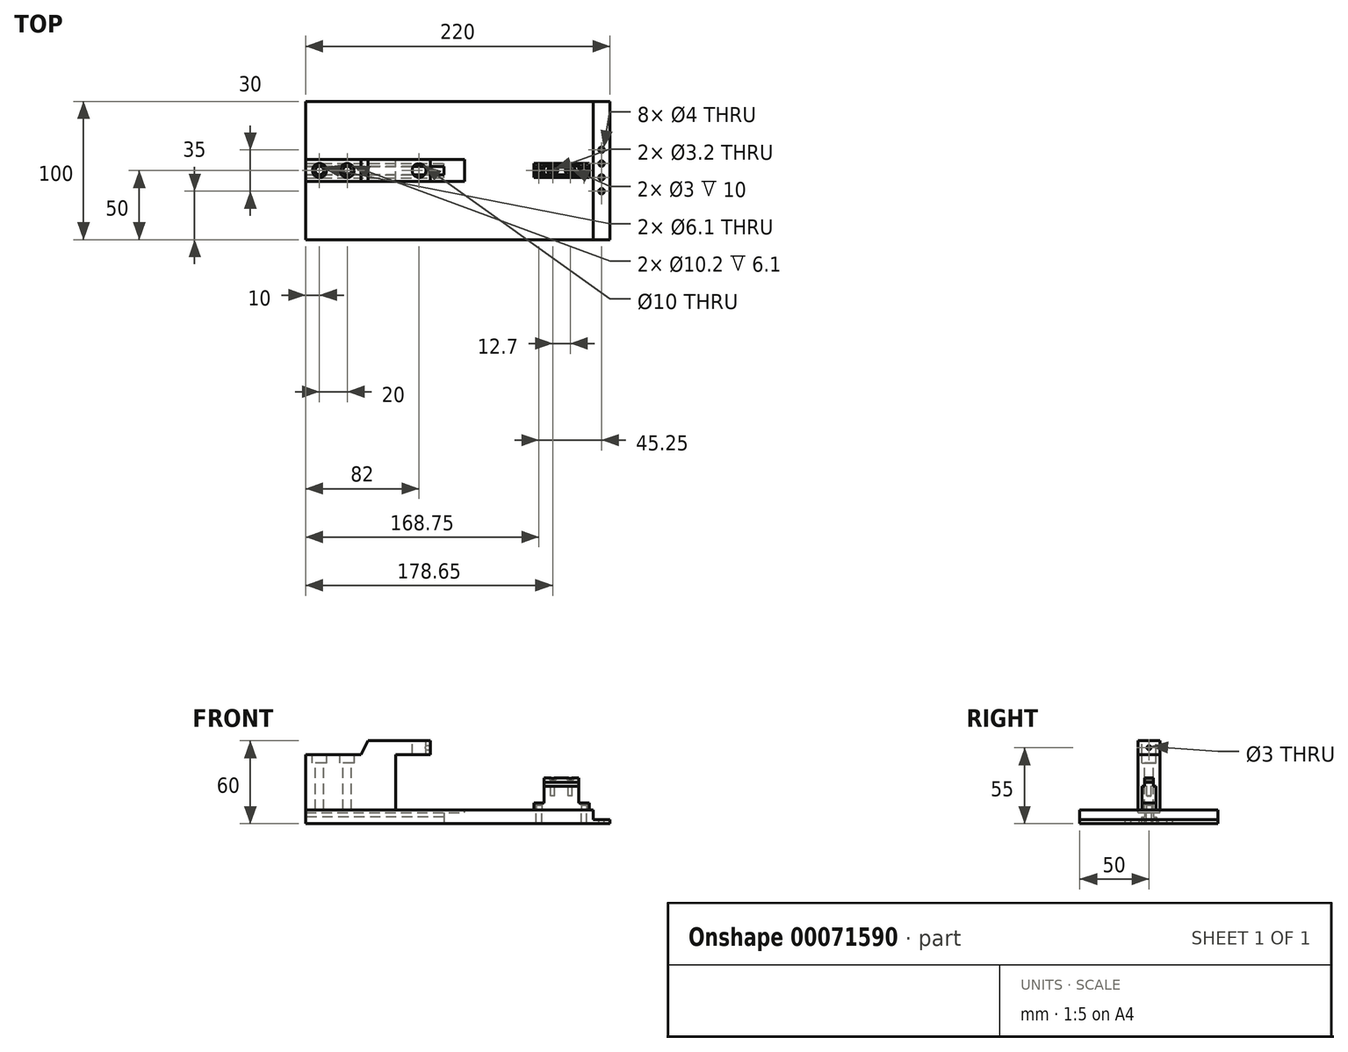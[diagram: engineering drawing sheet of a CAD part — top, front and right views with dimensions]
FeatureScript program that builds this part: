
annotation { "Feature Type Name" : "Feature", "Feature Type Description" : "" }
export const myFeature = defineFeature(function(context is Context, id is Id, definition is map)
    precondition{}
    {
        {
            var Q0;
            Q0=qCreatedBy(makeId("Top.planeOp"),FACE);
            var sketch = newSketch(context, id + "F0", { "sketchPlane" : qUnion([Q0])});
            skLineSegment(sketch, "E0.bottom", {"start": v(0, 0) * mm, "end": v(220, 0) * mm});
            skLineSegment(sketch, "E0.top", {"start": v(0, 100) * mm, "end": v(220, 100) * mm});
            skLineSegment(sketch, "E0.left", {"start": v(0, 0) * mm, "end": v(0, 100) * mm});
            skLineSegment(sketch, "E0.right", {"start": v(220, 0) * mm, "end": v(220, 100) * mm});
            skSolve(sketch);
        }
        {
            var Q0;
            Q0 = qSketchRegion(id + "F0", true);
            extrude(context, id + "F1", {"entities" : qUnion([Q0]), "depth" : 10 * mm});
        }
        {
            var Q0;
            Q0=makeQuery(id+"F1.opExtrude","CAP_FACE",FACE,{"disambiguationData":[OSD([sQuery(id+"F0.wireOp",EDGE,"E0.bottom"),sQuery(id+"F0.wireOp",EDGE,"E0.top"),sQuery(id+"F0.wireOp",EDGE,"E0.left"),sQuery(id+"F0.wireOp",EDGE,"E0.right")])],"isStart":false});
            var sketch = newSketch(context, id + "F2", { "sketchPlane" : qUnion([Q0])});
            skLineSegment(sketch, "E1.bottom", {"start": v(165, 55.18) * mm, "end": v(205, 55.18) * mm});
            skLineSegment(sketch, "E1.top", {"start": v(165, 44.82) * mm, "end": v(205, 44.82) * mm});
            skLineSegment(sketch, "E1.left", {"start": v(165, 55.18) * mm, "end": v(165, 44.82) * mm});
            skLineSegment(sketch, "E1.right", {"start": v(205, 55.18) * mm, "end": v(205, 44.82) * mm});
            skCircle(sketch, "E2", {"center": v(168.75, 50) * mm, "radius": 2 * mm});
            skPoint(sketch, "E2.centerSnap0", {"position": v(165, 50) * mm});
            skCircle(sketch, "E3", {"center": v(201.25, 50) * mm, "radius": 2 * mm});
            skPoint(sketch, "E3.centerSnap0", {"position": v(205, 50) * mm});
            skSolve(sketch);
        }
        {
            var Q0;
            Q0 = qSketchRegion(id + "F2", true);
            extrude(context, id + "F3", {"entities" : qUnion([Q0]), "depth" : 20 * mm});
        }
        {
            var Q0;
            Q0=makeQuery(id+"F3.opExtrude","SWEPT_FACE",FACE,{"disambiguationData":[OSD([sQuery(id+"F2.wireOp",EDGE,"E1.top")])]});
            var sketch = newSketch(context, id + "F4", { "sketchPlane" : qUnion([Q0])});
            skLineSegment(sketch, "E4.bottom", {"start": v(165, 30) * mm, "end": v(172.5, 30) * mm});
            skLineSegment(sketch, "E4.top", {"start": v(165, 15) * mm, "end": v(172.5, 15) * mm});
            skLineSegment(sketch, "E4.left", {"start": v(165, 30) * mm, "end": v(165, 15) * mm});
            skLineSegment(sketch, "E4.right", {"start": v(172.5, 30) * mm, "end": v(172.5, 15) * mm});
            skLineSegment(sketch, "E5.right", {"start": v(205, 30) * mm, "end": v(205, 15) * mm});
            skLineSegment(sketch, "E5.bottom", {"start": v(197.5, 30) * mm, "end": v(205, 30) * mm});
            skLineSegment(sketch, "E5.left", {"start": v(197.5, 30) * mm, "end": v(197.5, 15) * mm});
            skLineSegment(sketch, "E5.top", {"start": v(197.5, 15) * mm, "end": v(205, 15) * mm});
            skSolve(sketch);
        }
        {
            var Q0;
            Q0 = qSketchRegion(id + "F4", true);
            extrude(context, id + "F5", {"entities" : qUnion([Q0]), "operationType" : NewBodyOperationType.REMOVE, "endBound" : BoundingType.THROUGH_ALL, "oppositeDirection" : true, "depth" : 25 * mm});
        }
        {
            var Q0;
            Q0=makeQuery(id+"F3.opExtrude","CAP_FACE",FACE,{"disambiguationData":[OSD([sQuery(id+"F2.wireOp",EDGE,"E1.bottom"),sQuery(id+"F2.wireOp",EDGE,"E1.top"),sQuery(id+"F2.wireOp",EDGE,"E1.left"),sQuery(id+"F2.wireOp",EDGE,"E1.right")])],"isStart":false});
            var sketch = newSketch(context, id + "F6", { "sketchPlane" : qUnion([Q0])});
            skCircle(sketch, "E6", {"center": v(178.65, 50) * mm, "radius": 1.5 * mm});
            skCircle(sketch, "E7", {"center": v(191.35, 50) * mm, "radius": 1.5 * mm});
            skLineSegment(sketch, "E8", {"start": v(172.5, 50) * mm, "end": v(197.5, 50) * mm, "construction": true});
            skSolve(sketch);
        }
        {
            var Q0;
            Q0 = qSketchRegion(id + "F6", true);
            extrude(context, id + "F7", {"entities" : qUnion([Q0]), "operationType" : NewBodyOperationType.REMOVE, "oppositeDirection" : true, "depth" : 10 * mm});
        }
        {
            var Q0;
            Q0=makeQuery(id+"F3.opExtrude","CAP_FACE",FACE,{"disambiguationData":[OSD([sQuery(id+"F2.wireOp",EDGE,"E1.bottom"),sQuery(id+"F2.wireOp",EDGE,"E1.top"),sQuery(id+"F2.wireOp",EDGE,"E1.left"),sQuery(id+"F2.wireOp",EDGE,"E1.right")])],"isStart":false});
            var sketch = newSketch(context, id + "F8", { "sketchPlane" : qUnion([Q0])});
            skLineSegment(sketch, "E9.bottom", {"start": v(172.5, 55.18) * mm, "end": v(197.5, 55.18) * mm});
            skLineSegment(sketch, "E9.top", {"start": v(172.5, 53.17) * mm, "end": v(197.5, 53.17) * mm});
            skLineSegment(sketch, "E9.left", {"start": v(172.5, 55.18) * mm, "end": v(172.5, 53.17) * mm});
            skLineSegment(sketch, "E9.right", {"start": v(197.5, 55.18) * mm, "end": v(197.5, 53.17) * mm});
            skLineSegment(sketch, "E10.bottom", {"start": v(172.5, 44.82) * mm, "end": v(197.5, 44.82) * mm});
            skLineSegment(sketch, "E10.top", {"start": v(172.5, 46.83) * mm, "end": v(197.5, 46.83) * mm});
            skLineSegment(sketch, "E10.left", {"start": v(172.5, 44.82) * mm, "end": v(172.5, 46.82) * mm});
            skLineSegment(sketch, "E10.right", {"start": v(197.5, 44.82) * mm, "end": v(197.5, 46.82) * mm});
            skSolve(sketch);
        }
        {
            var Q0;
            Q0 = qSketchRegion(id + "F8", true);
            extrude(context, id + "F9", {"entities" : qUnion([Q0]), "operationType" : NewBodyOperationType.REMOVE, "oppositeDirection" : true, "depth" : 3 * mm});
        }
        {
            var Q0;
            Q0=makeQuery(id+"F5.boolean.opBoolean","INTERSECT",EDGE,{"derivedFrom":[makeQuery(id+"F3.opExtrude","SWEPT_FACE",FACE,{"disambiguationData":[OSD([sQuery(id+"F2.wireOp",EDGE,"E2")])]}),makeQuery(id+"F5.opExtrude","SWEPT_FACE",FACE,{"disambiguationData":[OSD([sQuery(id+"F4.wireOp",EDGE,"E4.top")])]})]});
            var Q1;
            Q1=makeQuery(id+"F5.boolean.opBoolean","INTERSECT",EDGE,{"derivedFrom":[makeQuery(id+"F3.opExtrude","SWEPT_FACE",FACE,{"disambiguationData":[OSD([sQuery(id+"F2.wireOp",EDGE,"E3")])]}),makeQuery(id+"F5.opExtrude","SWEPT_FACE",FACE,{"disambiguationData":[OSD([sQuery(id+"F4.wireOp",EDGE,"E5.top")])]})]});
            chamfer(context, id + "F10", {"entities" : qUnion([Q0, Q1]), "width" : 1.5 * mm, "tangentPropagation" : true});
        }
        {
            var Q0;
            Q0=makeQuery(id+"F1.opExtrude","CAP_FACE",FACE,{"disambiguationData":[OSD([sQuery(id+"F0.wireOp",EDGE,"E0.bottom"),sQuery(id+"F0.wireOp",EDGE,"E0.top"),sQuery(id+"F0.wireOp",EDGE,"E0.left"),sQuery(id+"F0.wireOp",EDGE,"E0.right")])],"isStart":false});
            var sketch = newSketch(context, id + "F11", { "sketchPlane" : qUnion([Q0])});
            skCircle(sketch, "E11.0", {"center": v(168.75, 50) * mm, "radius": 2 * mm});
            skCircle(sketch, "E11.1", {"center": v(201.25, 50) * mm, "radius": 2 * mm});
            skCircle(sketch, "E12", {"center": v(214, 65) * mm, "radius": 2 * mm});
            skCircle(sketch, "E13", {"center": v(214, 55) * mm, "radius": 2 * mm});
            skCircle(sketch, "E14", {"center": v(214, 45) * mm, "radius": 2 * mm});
            skCircle(sketch, "E15", {"center": v(214, 35) * mm, "radius": 2 * mm});
            skSolve(sketch);
        }
        {
            var Q0;
            Q0 = qSketchRegion(id + "F11", true);
            extrude(context, id + "F12", {"entities" : qUnion([Q0]), "operationType" : NewBodyOperationType.REMOVE, "endBound" : BoundingType.THROUGH_ALL, "oppositeDirection" : true, "depth" : 5 * mm});
        }
        {
            var Q0;
            Q0=makeQuery(id+"F3.opExtrude","CAP_FACE",FACE,{"disambiguationData":[OSD([sQuery(id+"F2.wireOp",EDGE,"E1.bottom"),sQuery(id+"F2.wireOp",EDGE,"E1.top"),sQuery(id+"F2.wireOp",EDGE,"E1.left"),sQuery(id+"F2.wireOp",EDGE,"E1.right"),sQuery(id+"F2.wireOp",EDGE,"E2"),sQuery(id+"F2.wireOp",EDGE,"E3")])],"isStart":false});
            var sketch = newSketch(context, id + "F13", { "sketchPlane" : qUnion([Q0])});
            skLineSegment(sketch, "E16.bottom", {"start": v(172.5, 53.17) * mm, "end": v(197.5, 53.17) * mm});
            skLineSegment(sketch, "E16.top", {"start": v(172.5, 46.83) * mm, "end": v(197.5, 46.83) * mm});
            skLineSegment(sketch, "E16.left", {"start": v(172.5, 53.17) * mm, "end": v(172.5, 46.83) * mm});
            skLineSegment(sketch, "E16.right", {"start": v(197.5, 53.17) * mm, "end": v(197.5, 46.83) * mm});
            skCircle(sketch, "E17", {"center": v(178.65, 50) * mm, "radius": 1.6 * mm});
            skCircle(sketch, "E18", {"center": v(191.35, 50) * mm, "radius": 1.6 * mm});
            skSolve(sketch);
        }
        {
            var Q0;
            Q0 = qSketchRegion(id + "F13", true);
            extrude(context, id + "F14", {"entities" : qUnion([Q0]), "depth" : 3.25 * mm});
        }
        {
            var Q0;
            Q0=makeQuery(id+"F14.opExtrude","CAP_EDGE",EDGE,{"disambiguationData":[OSD([sQuery(id+"F13.wireOp",EDGE,"E17")])],"isStart":false});
            var Q1;
            Q1=makeQuery(id+"F14.opExtrude","CAP_EDGE",EDGE,{"disambiguationData":[OSD([sQuery(id+"F13.wireOp",EDGE,"E18")])],"isStart":false});
            chamfer(context, id + "F15", {"entities" : qUnion([Q0, Q1]), "width" : 2 * mm, "tangentPropagation" : true});
        }
        {
            var Q0;
            Q0=makeQuery(id+"F1.opExtrude","CAP_FACE",FACE,{"disambiguationData":[OSD([sQuery(id+"F0.wireOp",EDGE,"E0.bottom"),sQuery(id+"F0.wireOp",EDGE,"E0.top"),sQuery(id+"F0.wireOp",EDGE,"E0.left"),sQuery(id+"F0.wireOp",EDGE,"E0.right")])],"isStart":true});
            var sketch = newSketch(context, id + "F16", { "sketchPlane" : qUnion([Q0])});
            skLineSegment(sketch, "E19.bottom", {"start": v(0, -46.95) * mm, "end": v(100, -46.95) * mm});
            skLineSegment(sketch, "E19.top", {"start": v(0, -53.05) * mm, "end": v(100, -53.05) * mm});
            skLineSegment(sketch, "E19.left", {"start": v(0, -46.95) * mm, "end": v(0, -53.05) * mm});
            skLineSegment(sketch, "E19.right", {"start": v(100, -46.95) * mm, "end": v(100, -53.05) * mm});
            skSolve(sketch);
        }
        {
            var Q0;
            Q0 = qSketchRegion(id + "F16", true);
            extrude(context, id + "F17", {"entities" : qUnion([Q0]), "operationType" : NewBodyOperationType.REMOVE, "oppositeDirection" : true, "depth" : 25 * mm});
        }
        {
            var Q0;
            Q0=makeQuery(id+"F1.opExtrude","CAP_FACE",FACE,{"disambiguationData":[OSD([sQuery(id+"F0.wireOp",EDGE,"E0.bottom"),sQuery(id+"F0.wireOp",EDGE,"E0.top"),sQuery(id+"F0.wireOp",EDGE,"E0.left"),sQuery(id+"F0.wireOp",EDGE,"E0.right")])],"isStart":true});
            var sketch = newSketch(context, id + "F18", { "sketchPlane" : qUnion([Q0])});
            skLineSegment(sketch, "E20.bottom", {"start": v(0, -44.75) * mm, "end": v(100, -44.75) * mm});
            skLineSegment(sketch, "E20.top", {"start": v(0, -55.25) * mm, "end": v(100, -55.25) * mm});
            skLineSegment(sketch, "E20.left", {"start": v(0, -44.75) * mm, "end": v(0, -55.25) * mm});
            skLineSegment(sketch, "E20.right", {"start": v(100, -44.75) * mm, "end": v(100, -55.25) * mm});
            skSolve(sketch);
        }
        {
            var Q0;
            Q0 = qSketchRegion(id + "F18", true);
            extrude(context, id + "F19", {"entities" : qUnion([Q0]), "operationType" : NewBodyOperationType.REMOVE, "oppositeDirection" : true, "depth" : 5 * mm});
        }
        {
            var Q0;
            Q0=makeQuery(id+"F1.opExtrude","CAP_FACE",FACE,{"disambiguationData":[OSD([sQuery(id+"F0.wireOp",EDGE,"E0.bottom"),sQuery(id+"F0.wireOp",EDGE,"E0.top"),sQuery(id+"F0.wireOp",EDGE,"E0.left"),sQuery(id+"F0.wireOp",EDGE,"E0.right")])],"isStart":false});
            var sketch = newSketch(context, id + "F20", { "sketchPlane" : qUnion([Q0])});
            skCircle(sketch, "E21", {"center": v(168.75, 50) * mm, "radius": 2 * mm});
            skCircle(sketch, "E22", {"center": v(201.25, 50) * mm, "radius": 2 * mm});
            skSolve(sketch);
        }
        {
            var Q0;
            Q0 = qSketchRegion(id + "F20", true);
            extrude(context, id + "F21", {"entities" : qUnion([Q0]), "operationType" : NewBodyOperationType.REMOVE, "endBound" : BoundingType.THROUGH_ALL, "oppositeDirection" : true, "depth" : 25 * mm});
        }
        {
            var Q0;
            Q0=qCreatedBy(makeId("Front.planeOp"),FACE);
            cPlane(context, id + "F22", {"entities" : qUnion([Q0]), "cplaneType" : CPlaneType.OFFSET, "offset" : 50 * mm, "oppositeDirection" : true, "width" : 150 * mm, "height" : 150 * mm});
        }
        {
            var Q0;
            Q0=qCreatedBy(id+"F22.planeOp",FACE);
            var sketch = newSketch(context, id + "F23", { "sketchPlane" : qUnion([Q0])});
            skLineSegment(sketch, "E23", {"start": v(0, 10) * mm, "end": v(0, 50) * mm});
            skLineSegment(sketch, "E24", {"start": v(0, 50) * mm, "end": v(40, 50) * mm});
            skLineSegment(sketch, "E25", {"start": v(40, 50) * mm, "end": v(45, 60) * mm});
            skLineSegment(sketch, "E26", {"start": v(45, 60) * mm, "end": v(90, 60) * mm});
            skLineSegment(sketch, "E27", {"start": v(90, 60) * mm, "end": v(90, 50) * mm});
            skLineSegment(sketch, "E28", {"start": v(90, 50) * mm, "end": v(65, 50) * mm});
            skLineSegment(sketch, "E29", {"start": v(65, 50) * mm, "end": v(65, 10) * mm});
            skLineSegment(sketch, "E30", {"start": v(65, 10) * mm, "end": v(0, 10) * mm});
            skSolve(sketch);
        }
        {
            var Q0;
            Q0 = qSketchRegion(id + "F23", true);
            extrude(context, id + "F24", {"entities" : qUnion([Q0]), "endBound" : BoundingType.SYMMETRIC, "depth" : 16 * mm});
        }
        {
            var Q0;
            Q0=makeQuery(id+"F24.opExtrude","SWEPT_FACE",FACE,{"disambiguationData":[OSD([sQuery(id+"F23.wireOp",EDGE,"E24")])]});
            var sketch = newSketch(context, id + "F25", { "sketchPlane" : qUnion([Q0])});
            skCircle(sketch, "E31", {"center": v(10, 50) * mm, "radius": 3.05 * mm});
            skPoint(sketch, "E31.centerSnap0", {"position": v(0, 50) * mm});
            skCircle(sketch, "E32", {"center": v(30, 50) * mm, "radius": 3.05 * mm});
            skSolve(sketch);
        }
        {
            var Q0;
            Q0 = qSketchRegion(id + "F25", true);
            extrude(context, id + "F26", {"entities" : qUnion([Q0]), "operationType" : NewBodyOperationType.REMOVE, "endBound" : BoundingType.UP_TO_NEXT, "oppositeDirection" : true, "depth" : 25 * mm});
        }
        {
            var Q0;
            Q0=makeQuery(id+"F24.opExtrude","SWEPT_FACE",FACE,{"disambiguationData":[OSD([sQuery(id+"F23.wireOp",EDGE,"E24")])]});
            var sketch = newSketch(context, id + "F27", { "sketchPlane" : qUnion([Q0])});
            skCircle(sketch, "E33", {"center": v(10, 50) * mm, "radius": 5.1 * mm});
            skCircle(sketch, "E34", {"center": v(30, 50) * mm, "radius": 5.1 * mm});
            skSolve(sketch);
        }
        {
            var Q0;
            Q0 = qSketchRegion(id + "F27", true);
            extrude(context, id + "F28", {"entities" : qUnion([Q0]), "operationType" : NewBodyOperationType.REMOVE, "oppositeDirection" : true, "depth" : 6.1 * mm});
        }
        {
            var Q0;
            Q0=makeQuery(id+"F24.opExtrude","SWEPT_FACE",FACE,{"disambiguationData":[OSD([sQuery(id+"F23.wireOp",EDGE,"E26")])]});
            var sketch = newSketch(context, id + "F29", { "sketchPlane" : qUnion([Q0])});
            skCircle(sketch, "E35", {"center": v(82, 50) * mm, "radius": 5 * mm});
            skPoint(sketch, "E35.centerSnap0", {"position": v(90, 50) * mm});
            skSolve(sketch);
        }
        {
            var Q0;
            Q0 = qSketchRegion(id + "F29", true);
            extrude(context, id + "F30", {"entities" : qUnion([Q0]), "operationType" : NewBodyOperationType.REMOVE, "endBound" : BoundingType.UP_TO_NEXT, "oppositeDirection" : true, "depth" : 25 * mm});
        }
        {
            var Q0;
            Q0=makeQuery(id+"F24.opExtrude","SWEPT_FACE",FACE,{"disambiguationData":[OSD([sQuery(id+"F23.wireOp",EDGE,"E27")])]});
            var sketch = newSketch(context, id + "F31", { "sketchPlane" : qUnion([Q0])});
            skCircle(sketch, "E36", {"center": v(50, 55) * mm, "radius": 1.5 * mm});
            skPoint(sketch, "E36.centerSnap0", {"position": v(42, 55) * mm});
            skPoint(sketch, "E36.centerSnap1", {"position": v(50, 60) * mm});
            skSolve(sketch);
        }
        {
            var Q0;
            Q0 = qSketchRegion(id + "F31", true);
            extrude(context, id + "F32", {"entities" : qUnion([Q0]), "operationType" : NewBodyOperationType.REMOVE, "endBound" : BoundingType.UP_TO_NEXT, "oppositeDirection" : true, "depth" : 25 * mm});
        }
        {
            var Q0;
            Q0=makeQuery(id+"F1.opExtrude","CAP_FACE",FACE,{"disambiguationData":[OSD([sQuery(id+"F0.wireOp",EDGE,"E0.bottom"),sQuery(id+"F0.wireOp",EDGE,"E0.top"),sQuery(id+"F0.wireOp",EDGE,"E0.left"),sQuery(id+"F0.wireOp",EDGE,"E0.right")])],"isStart":false});
            var sketch = newSketch(context, id + "F33", { "sketchPlane" : qUnion([Q0])});
            skLineSegment(sketch, "E37.bottom", {"start": v(220, 100) * mm, "end": v(208, 100) * mm});
            skLineSegment(sketch, "E37.top", {"start": v(220, 0) * mm, "end": v(208, 0) * mm});
            skLineSegment(sketch, "E37.left", {"start": v(220, 100) * mm, "end": v(220, 0) * mm});
            skLineSegment(sketch, "E37.right", {"start": v(208, 100) * mm, "end": v(208, 0) * mm});
            skSolve(sketch);
        }
        {
            var Q0;
            Q0 = qSketchRegion(id + "F33", true);
            extrude(context, id + "F34", {"entities" : qUnion([Q0]), "operationType" : NewBodyOperationType.REMOVE, "oppositeDirection" : true, "depth" : 7 * mm});
        }
        {
            var Q0;
            Q0=makeQuery(id+"F1.opExtrude","CAP_FACE",FACE,{"disambiguationData":[OSD([sQuery(id+"F0.wireOp",EDGE,"E0.bottom"),sQuery(id+"F0.wireOp",EDGE,"E0.top"),sQuery(id+"F0.wireOp",EDGE,"E0.left"),sQuery(id+"F0.wireOp",EDGE,"E0.right")])],"isStart":false});
            var sketch = newSketch(context, id + "F35", { "sketchPlane" : qUnion([Q0])});
            skLineSegment(sketch, "E38.bottom", {"start": v(0, 42) * mm, "end": v(115, 42) * mm});
            skLineSegment(sketch, "E38.top", {"start": v(0, 58) * mm, "end": v(115, 58) * mm});
            skLineSegment(sketch, "E38.left", {"start": v(0, 42) * mm, "end": v(0, 58) * mm});
            skLineSegment(sketch, "E38.right", {"start": v(115, 42) * mm, "end": v(115, 58) * mm});
            skLineSegment(sketch, "E39", {"start": v(208, 50) * mm, "end": v(-17.6, 50) * mm, "construction": true});
            skSolve(sketch);
        }
        {
            var Q0;
            Q0 = qSketchRegion(id + "F35", true);
            extrude(context, id + "F36", {"entities" : qUnion([Q0]), "operationType" : NewBodyOperationType.REMOVE, "oppositeDirection" : true, "depth" : 2 * mm});
        }
    });
